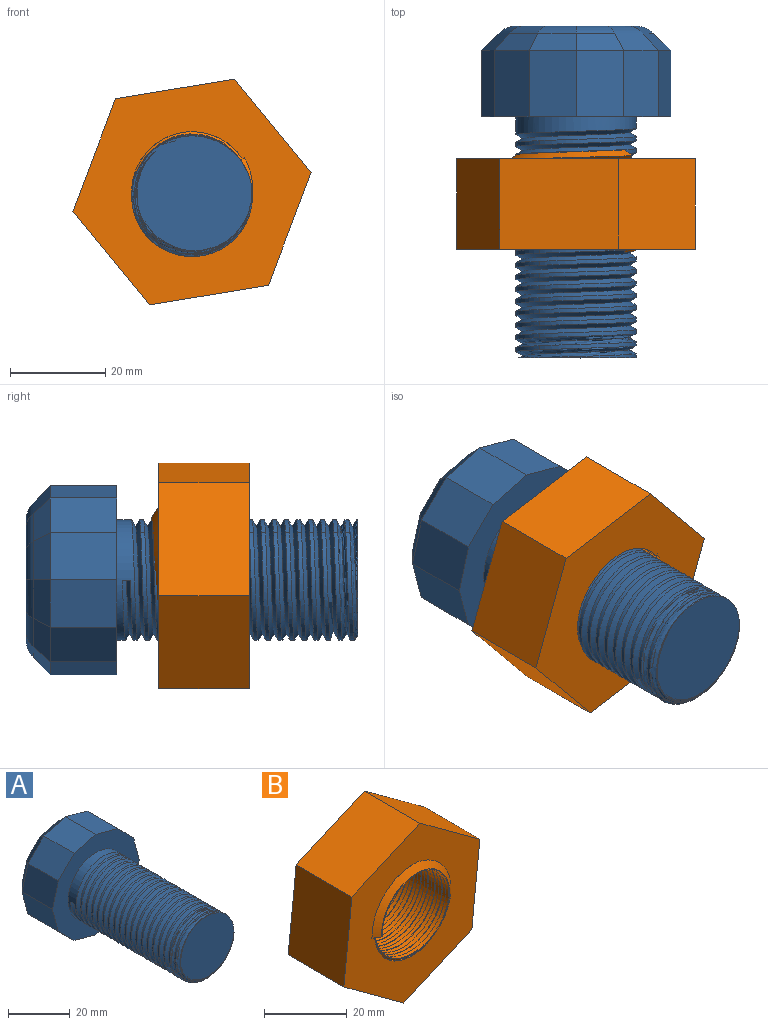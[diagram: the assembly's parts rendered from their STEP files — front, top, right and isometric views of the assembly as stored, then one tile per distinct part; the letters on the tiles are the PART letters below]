
ASSEMBLY  parts=2 mates=1
PART A: 61 faces, bbox 39.9x71.2x39.9 mm
  f0: cylinder r=12.7mm len=25.4mm, axis (0,1,0), area 56.3mm2, adj f1,f19,f21,f22
  f1: cylinder r=12.7mm len=25.4mm, axis (0,1,0), area 67.6mm2, adj f0,f2,f21,f22
  f2: cylinder r=12.7mm len=25.4mm, axis (0,1,0), area 67.5mm2, adj f1,f3,f21,f22
  f3: cylinder r=12.7mm len=25.4mm, axis (0,1,0), area 67.6mm2, adj f2,f4,f21,f22
  f4: cylinder r=12.7mm len=25.4mm, axis (0,1,0), area 67.6mm2, adj f3,f5,f21,f22
  f5: cylinder r=12.7mm len=25.4mm, axis (0,1,0), area 67.6mm2, adj f4,f6,f21,f22
  f6: cylinder r=12.7mm len=25.4mm, axis (0,1,0), area 67.6mm2, adj f5,f7,f21,f22
  f7: cylinder r=12.7mm len=25.4mm, axis (0,1,0), area 67.6mm2, adj f6,f8,f21,f22
  f8: cylinder r=12.7mm len=25.4mm, axis (0,1,0), area 67.6mm2, adj f7,f9,f21,f22
  f9: cylinder r=12.7mm len=25.4mm, axis (0,1,0), area 67.6mm2, adj f8,f10,f21,f22
  f10: cylinder r=12.7mm len=25.4mm, axis (0,1,0), area 67.6mm2, adj f9,f11,f21,f22
  f11: cylinder r=12.7mm len=25.4mm, axis (0,1,0), area 67.5mm2, adj f10,f12,f21,f22
  f12: cylinder r=12.7mm len=25.4mm, axis (0,1,0), area 67.6mm2, adj f11,f13,f21,f22
  f13: cylinder r=12.7mm len=25.4mm, axis (0,1,0), area 67.6mm2, adj f12,f14,f21,f22
  f14: cylinder r=12.7mm len=25.4mm, axis (0,1,0), area 67.6mm2, adj f13,f15,f21,f22
  f15: cylinder r=12.7mm len=25.4mm, axis (0,1,0), area 67.6mm2, adj f14,f16,f21,f22
  f16: cylinder r=12.7mm len=25.4mm, axis (0,1,0), area 67.6mm2, adj f15,f17,f21,f22
  f17: cylinder r=12.7mm len=25.4mm, axis (0,1,0), area 67.6mm2, adj f16,f18,f21,f22
  f18: cylinder r=12.7mm len=25.4mm, axis (0,1,0), area 256.2mm2, adj f17,f20,f21,f22,f36
  f19: plane 24.72x24.23mm, normal (0,-1,0), area 469.2mm2, adj f0,f21,f22
  f20: plane 1.69x1.47mm, normal (0,0,-1), area 1.2mm2, adj f18,f21,f22
  f21: bspline ~50.82x26.76mm, area 2465.3mm2, adj f0,f1,f2,f3,f4,f5,f6,f7
  f22: bspline ~50.1x26.66mm, area 2422.1mm2, adj f0,f1,f2,f3,f4,f5,f6,f7
  f23: plane 13.97x9.98mm, normal (-0.97,0,-0.26), area 144.1mm2, adj f24,f34,f36,f48
  f24: plane 13.97x9.96mm, normal (-0.96,0,0.26), area 144.1mm2, adj f23,f25,f36,f46
  f25: plane 13.97x7.32mm, normal (-0.7,0,0.71), area 144.1mm2, adj f24,f26,f36,f44
  f26: plane 13.97x9.98mm, normal (-0.26,0,0.97), area 144.1mm2, adj f25,f27,f36,f42
  f27: plane 13.97x9.96mm, normal (0.26,0,0.96), area 144.1mm2, adj f26,f28,f36,f40
  f28: plane 13.97x7.32mm, normal (0.71,0,0.7), area 144.1mm2, adj f27,f29,f36,f38
  f29: plane 13.97x9.98mm, normal (0.97,0,0.26), area 144.1mm2, adj f28,f30,f36,f37
  f30: plane 13.97x9.96mm, normal (0.96,0,-0.26), area 144.1mm2, adj f29,f31,f36,f39
  f31: plane 13.97x7.32mm, normal (0.7,0,-0.71), area 144.1mm2, adj f30,f32,f36,f41
  f32: plane 13.97x9.98mm, normal (0.26,0,-0.97), area 144.1mm2, adj f31,f33,f36,f43
  f33: plane 13.97x9.96mm, normal (-0.26,0,-0.96), area 144.1mm2, adj f32,f34,f36,f45
  f34: plane 13.97x7.32mm, normal (-0.71,0,-0.7), area 144.1mm2, adj f23,f33,f36,f47
  f35: plane 24.99x24.99mm, normal (0,1,0), area 468.4mm2, adj f49,f50,f51,f52,f53,f54,f55,f56
  f36: plane 39.87x39.87mm, normal (0,-1,0), area 685.2mm2, adj f18,f23,f24,f25,f26,f27,f28,f29
  f37: plane 9.98x5.86mm, normal (0.68,0.71,0.18), area 47.5mm2, adj f29,f38,f39,f49
  f38: plane 9.17x9.14mm, normal (0.5,0.71,0.5), area 47.5mm2, adj f28,f37,f40,f51
  f39: plane 9.97x5.92mm, normal (0.68,0.71,-0.19), area 47.5mm2, adj f30,f37,f41,f50
  f40: plane 9.97x5.92mm, normal (0.19,0.71,0.68), area 47.5mm2, adj f27,f38,f42,f53
  f41: plane 9.17x9.14mm, normal (0.5,0.71,-0.5), area 47.5mm2, adj f31,f39,f43,f52
  f42: plane 9.98x5.86mm, normal (-0.18,0.71,0.68), area 47.5mm2, adj f26,f40,f44,f55
  f43: plane 9.98x5.86mm, normal (0.18,0.71,-0.68), area 47.5mm2, adj f32,f41,f45,f54
  f44: plane 9.17x9.14mm, normal (-0.5,0.71,0.5), area 47.5mm2, adj f25,f42,f46,f57
  f45: plane 9.97x5.92mm, normal (-0.19,0.71,-0.68), area 47.5mm2, adj f33,f43,f47,f56
  f46: plane 9.97x5.92mm, normal (-0.68,0.71,0.19), area 47.5mm2, adj f24,f44,f48,f59
  f47: plane 9.17x9.14mm, normal (-0.5,0.71,-0.5), area 47.5mm2, adj f34,f45,f48,f58
  f48: plane 9.98x5.86mm, normal (-0.68,0.71,-0.18), area 47.5mm2, adj f23,f46,f47,f60
  f49: cylinder r=5.08mm len=9.03mm, axis (-0.26,0,0.97), area 29.6mm2, adj f35,f37,f50,f51
  f50: cylinder r=5.08mm len=9.04mm, axis (0.26,0,0.96), area 29.6mm2, adj f35,f39,f49,f52
  f51: cylinder r=5.08mm len=8.49mm, axis (-0.7,0,0.71), area 29.6mm2, adj f35,f38,f49,f53
  f52: cylinder r=5.08mm len=8.49mm, axis (0.71,0,0.7), area 29.6mm2, adj f35,f41,f50,f54
  f53: cylinder r=5.08mm len=9.04mm, axis (-0.96,0,0.26), area 29.6mm2, adj f35,f40,f51,f55
  f54: cylinder r=5.08mm len=9.03mm, axis (0.97,0,0.26), area 29.6mm2, adj f35,f43,f52,f56
  f55: cylinder r=5.08mm len=9.03mm, axis (-0.97,0,-0.26), area 29.6mm2, adj f35,f42,f53,f57
  f56: cylinder r=5.08mm len=9.04mm, axis (0.96,0,-0.26), area 29.6mm2, adj f35,f45,f54,f58
  f57: cylinder r=5.08mm len=8.49mm, axis (-0.71,0,-0.7), area 29.6mm2, adj f35,f44,f55,f59
  f58: cylinder r=5.08mm len=8.49mm, axis (0.7,0,-0.71), area 29.6mm2, adj f35,f47,f56,f60
  f59: cylinder r=5.08mm len=9.04mm, axis (-0.26,0,-0.96), area 29.6mm2, adj f35,f46,f57,f60
  f60: cylinder r=5.08mm len=9.03mm, axis (0.26,0,-0.97), area 29.6mm2, adj f35,f48,f58,f59
PART B: 21 faces, bbox 47x22.1x51 mm
  f0: plane 50.59x46.56mm, normal (0,1,0), area 1167.3mm2, adj f1,f2,f3,f4,f5,f6,f7,f10
  f1: plane 25.25x19.05mm, normal (0.99,0,-0.11), area 483.9mm2, adj f0,f2,f6,f8
  f2: plane 20.5x19.05mm, normal (0.59,0,0.81), area 483.9mm2, adj f0,f1,f3,f8
  f3: plane 23.24x19.05mm, normal (-0.4,0,0.91), area 483.9mm2, adj f0,f2,f4,f8
  f4: plane 25.25x19.05mm, normal (-0.99,0,0.11), area 483.9mm2, adj f0,f3,f5,f8
  f5: plane 20.5x19.05mm, normal (-0.59,0,-0.81), area 483.9mm2, adj f0,f4,f6,f8
  f6: plane 23.24x19.05mm, normal (0.4,0,-0.91), area 483.9mm2, adj f0,f1,f5,f8
  f7: cylinder r=12.7mm len=25.4mm, axis (0,1,0), area 384.6mm2, adj f0,f8,f10,f11,f14,f20
  f8: plane 50.99x46.96mm, normal (0,-1,0), area 1120.9mm2, adj f1,f2,f3,f4,f5,f6,f7,f9
  f9: bspline ~19.83x14.56mm, area 15.4mm2, adj f8,f11,f20
  f10: plane 2.46x1.08mm, normal (0,0,1), area 1.4mm2, adj f0,f7,f12,f13,f14,f16,f17,f20
  f11: plane 2.46x2.2mm, normal (0,0,-1), area 2.7mm2, adj f7,f8,f9,f14,f16,f17,f18,f19
  f12: bspline ~28.23x24.45mm, area 12.1mm2, adj f10,f13,f14
  f13: cylinder r=12.09mm len=24.18mm, axis (0,-1,0), area 12.1mm2, adj f10,f12,f15,f16
  f14: bspline ~29.12x29.12mm, area 346.1mm2, adj f0,f7,f10,f11,f12,f20
  f15: bspline ~24.64x24.64mm, area 84.4mm2, adj f13,f16,f17,f18
  f16: bspline ~24.64x24.64mm, area 675.1mm2, adj f10,f11,f13,f15,f17
  f17: bspline ~24.64x24.64mm, area 675.1mm2, adj f10,f11,f15,f16,f18
  f18: bspline ~24.41x24.41mm, area 12.1mm2, adj f11,f15,f17,f19
  f19: bspline ~24.68x24.68mm, area 12.1mm2, adj f11,f18,f20
  f20: bspline ~29.12x29.12mm, area 415.1mm2, adj f7,f8,f9,f10,f11,f14,f19
PLACE A at identity fixed
PLACE B rot(axis=(0.29,0,-0.96),180deg) t=(-0.01,-27.93,0.88)mm
MATE cylindrical A.f19 <-> B.f8  axis (0,-1,0) through (0.25,-50.8,0.61)mm
